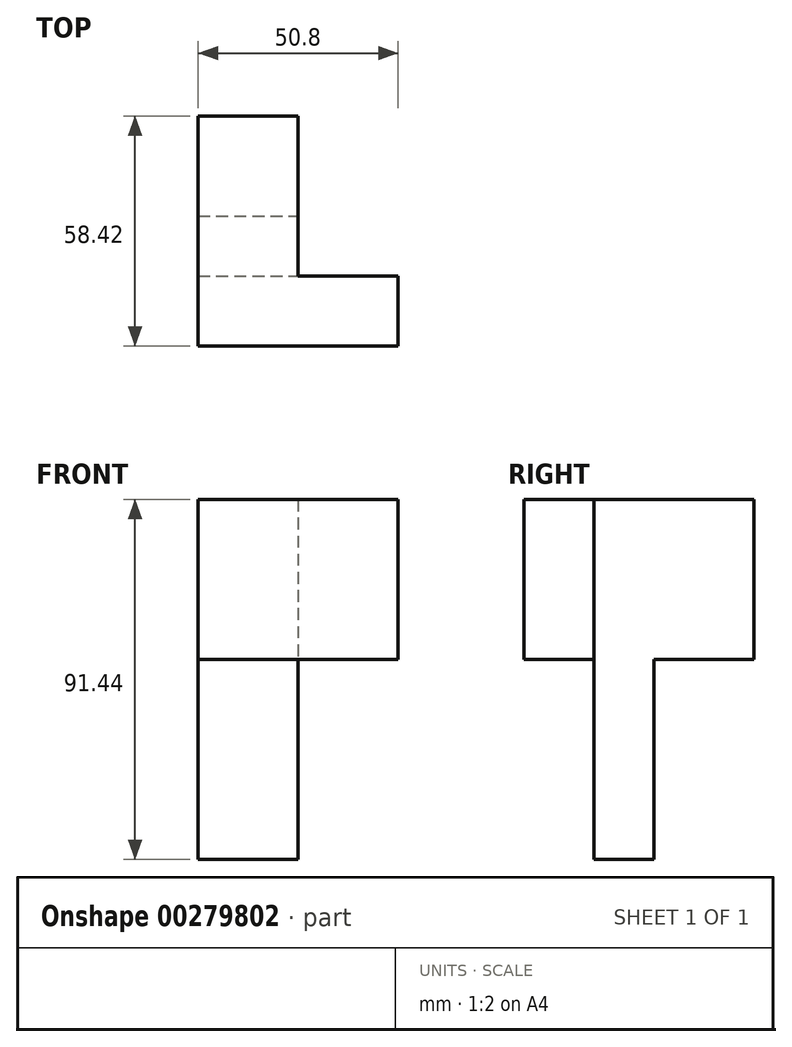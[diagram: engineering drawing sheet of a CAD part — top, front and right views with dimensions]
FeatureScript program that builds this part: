
annotation { "Feature Type Name" : "Feature", "Feature Type Description" : "" }
export const myFeature = defineFeature(function(context is Context, id is Id, definition is map)
    precondition{}
    {
        {
            var Q0;
            Q0=qCreatedBy(makeId("Right.planeOp"),FACE);
            var sketch = newSketch(context, id + "F0", { "sketchPlane" : qUnion([Q0])});
            skLineSegment(sketch, "E0.bottom", {"start": v(-11.76, 47.99) * mm, "end": v(-70.18, 47.99) * mm});
            skLineSegment(sketch, "E0.top", {"start": v(-11.76, 7.35) * mm, "end": v(-70.18, 7.35) * mm});
            skLineSegment(sketch, "E0.left", {"start": v(-11.76, 47.99) * mm, "end": v(-11.76, 7.35) * mm});
            skLineSegment(sketch, "E0.right", {"start": v(-70.18, 47.99) * mm, "end": v(-70.18, 7.35) * mm});
            skLineSegment(sketch, "E1", {"start": v(-52.4, 47.99) * mm, "end": v(-52.4, 7.35) * mm});
            skSolve(sketch);
        }
        {
            var Q0;
            {var subQ0=sQuery(id+"F0.wireOp",EDGE,"E0.left");Q0=makeQuery(id+"F0.imprint","IMPRINT",FACE,{"disambiguationData":[TD([[makeQuery(id+"F0.imprint","IMPRINT",EDGE,{"derivedFrom":subQ0}),-1.0]])]});}
            var Q1;
            {var subQ0=sQuery(id+"F0.wireOp",EDGE,"E0.right");Q1=makeQuery(id+"F0.imprint","IMPRINT",FACE,{"disambiguationData":[TD([[makeQuery(id+"F0.imprint","IMPRINT",EDGE,{"derivedFrom":subQ0}),1.0]])]});}
            extrude(context, id + "F1", {"entities" : qUnion([Q0, Q1]), "oppositeDirection" : true, "depth" : 25.4 * mm});
        }
        {
            var Q0;
            {var subQ0=sQuery(id+"F0.wireOp",EDGE,"E0.right");Q0=makeQuery(id+"F0.imprint","IMPRINT",FACE,{"disambiguationData":[TD([[makeQuery(id+"F0.imprint","IMPRINT",EDGE,{"derivedFrom":subQ0}),1.0]])]});}
            extrude(context, id + "F2", {"entities" : qUnion([Q0]), "operationType" : NewBodyOperationType.ADD, "depth" : 25.4 * mm});
        }
        {
            var Q0;
            {var subQ0=sQuery(id+"F0.wireOp",EDGE,"E0.top");Q0=makeQuery(id+"F2.boolean.opBoolean","MERGE",FACE,{"derivedFrom":[makeQuery(id+"F1.opExtrude","SWEPT_FACE",FACE,{"disambiguationData":[OSD([subQ0])]}),makeQuery(id+"F2.opExtrude","SWEPT_FACE",FACE,{"disambiguationData":[OSD([subQ0])]})]});}
            var sketch = newSketch(context, id + "F3", { "sketchPlane" : qUnion([Q0])});
            skLineSegment(sketch, "E2", {"start": v(-25.4, 37.16) * mm, "end": v(0, 37.16) * mm});
            skLineSegment(sketch, "E3", {"start": v(0, 52.4) * mm, "end": v(0, 70.18) * mm});
            skLineSegment(sketch, "E4", {"start": v(-25.4, 52.4) * mm, "end": v(0, 52.4) * mm});
            skSolve(sketch);
        }
        {
            var Q0;
            {var subQ0=sQuery(id+"F3.wireOp",EDGE,"E2");Q0=makeQuery(id+"F3.imprint","IMPRINT",FACE,{"disambiguationData":[TD([[makeQuery(id+"F3.imprint","IMPRINT",EDGE,{"derivedFrom":subQ0}),1.0]])]});}
            extrude(context, id + "F4", {"entities" : qUnion([Q0]), "operationType" : NewBodyOperationType.ADD, "depth" : 50.8 * mm});
        }
    });
